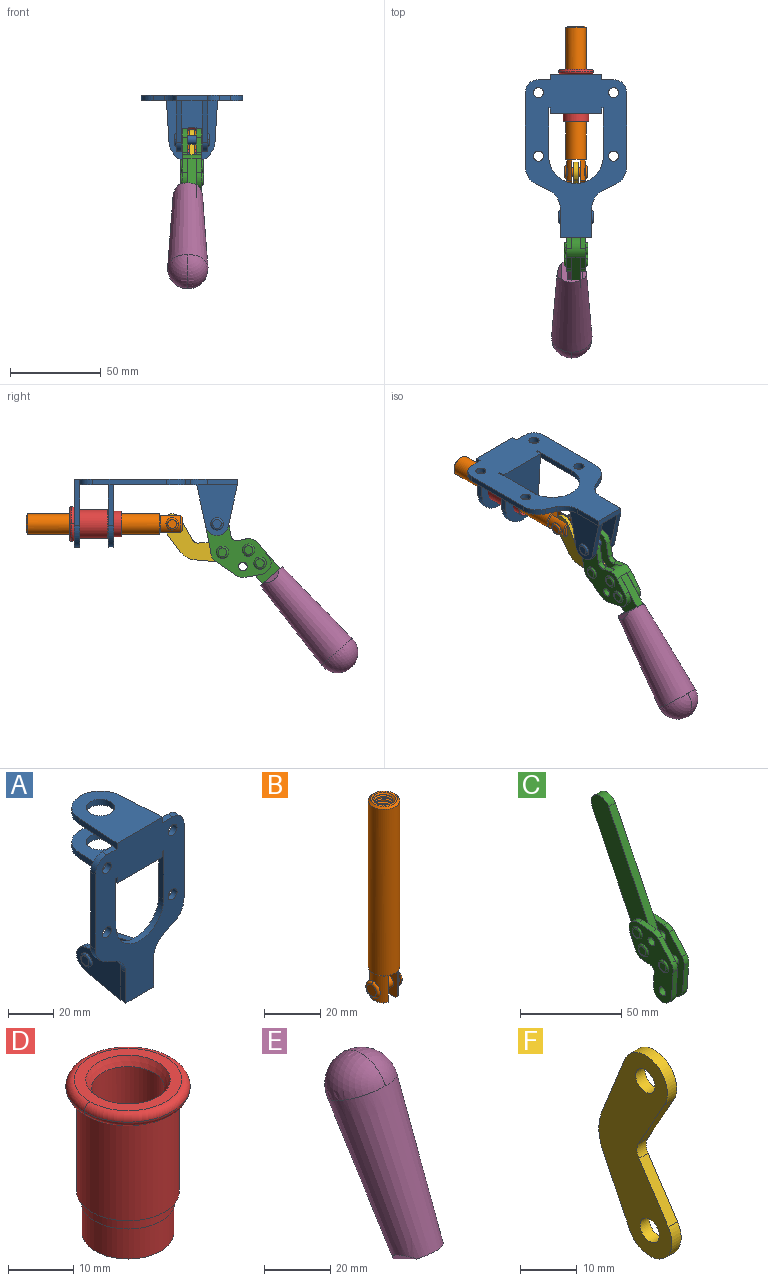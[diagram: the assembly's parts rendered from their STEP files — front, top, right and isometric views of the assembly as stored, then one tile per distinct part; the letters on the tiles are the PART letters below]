
ASSEMBLY  parts=6 mates=6
PART A: 55 faces, bbox 55.7x37.4x89.8 mm
  f0: torus R=2.41mm, axis (-1,0,0), area 15mm2, adj f11,f15,f25
  f1: torus R=2.41mm, axis (-1,0,0), area 15mm2, adj f10,f12,f22
  f2: cylinder r=2.78mm len=5.56mm, axis (0,-1,0), area 54.2mm2, adj f30,f54
  f3: cylinder r=14.99mm len=29.97mm, axis (0,-1,0), area 145.9mm2, adj f30,f49,f53,f54
  f4: cylinder r=2.78mm len=5.56mm, axis (0,-1,0), area 54.2mm2, adj f30,f54
  f5: cylinder r=2.78mm len=5.56mm, axis (0,-1,0), area 54.2mm2, adj f30,f54
  f6: cylinder r=2.78mm len=5.56mm, axis (0,-1,0), area 54.2mm2, adj f30,f54
  f7: cylinder r=6.35mm len=12.7mm, axis (0,0,1), area 123.6mm2, adj f27,f51
  f8: cylinder r=6.35mm len=12.7mm, axis (0,0,-1), area 124.7mm2, adj f21,f35
  f9: cylinder r=2.41mm len=11.18mm, axis (-1,0,0), area 169.4mm2, adj f16,f19
  f10: plane 4.83x4.83mm, normal (1,0,0), area 18.3mm2, adj f1,f12
  f11: plane 4.83x4.83mm, normal (-1,0,0), area 18.3mm2, adj f0,f15
  f12: torus R=2.41mm, axis (-1,0,0), area 15mm2, adj f1,f10,f22
  f13: cylinder r=6.35mm len=12.41mm, axis (1,0,0), area 53.4mm2, adj f18,f19,f22,f23
  f14: cylinder r=6.35mm len=12.41mm, axis (-1,0,0), area 53.4mm2, adj f16,f17,f24,f25
  f15: torus R=2.41mm, axis (-1,0,0), area 15mm2, adj f0,f11,f25
  f16: plane 27.86x22.35mm, normal (1,0,0), area 425.4mm2, adj f9,f14,f17,f24,f30
  f17: plane 22.86x4.97mm, normal (0,0.21,0.98), area 72.5mm2, adj f14,f16,f25,f30
  f18: plane 22.86x4.97mm, normal (0,0.21,0.98), area 72.5mm2, adj f13,f19,f22,f30
  f19: plane 27.86x22.35mm, normal (-1,0,0), area 425.4mm2, adj f9,f13,f18,f23,f30
  f20: cylinder r=12.7mm len=25.35mm, axis (0,0,-1), area 119.8mm2, adj f21,f34,f35,f36
  f21: plane 34.21x28.07mm, normal (0,0,-1), area 702.4mm2, adj f8,f20,f30,f34,f36
  f22: plane 27.96x22.45mm, normal (1,0,0), area 407.2mm2, adj f1,f12,f13,f18,f23,f30,f42,f43
  f23: plane 22.86x4.97mm, normal (0,0.21,-0.98), area 72.5mm2, adj f13,f19,f22,f44
  f24: plane 22.86x4.97mm, normal (0,0.21,-0.98), area 72.5mm2, adj f14,f16,f25,f44
  f25: plane 27.86x22.35mm, normal (-1,0,0), area 407.1mm2, adj f0,f14,f15,f17,f24,f30,f45,f46
  f26: plane 3.1x0.95mm, normal (0,0,-1), area 2.7mm2, adj f30,f49,f50,f54
  f27: plane 34.21x28.07mm, normal (0,0,1), area 702.4mm2, adj f7,f28,f30,f50,f52
  f28: cylinder r=12.7mm len=25.35mm, axis (0,0,1), area 118.8mm2, adj f27,f50,f51,f52
  f29: plane 3.1x0.95mm, normal (0,0,-1), area 2.7mm2, adj f30,f52,f53,f54
  f30: plane 86.54x55.63mm, normal (0,1,0), area 2362.9mm2, adj f2,f3,f4,f5,f6,f16,f17,f18
  f31: plane 40.56x3.1mm, normal (-1,0,0), area 125.7mm2, adj f30,f32,f48,f54
  f32: cylinder r=7.11mm len=7.11mm, axis (0,-1,0), area 34.6mm2, adj f30,f31,f33,f54
  f33: plane 6.67x3.1mm, normal (0,0,1), area 20.4mm2, adj f30,f32,f34,f54
  f34: plane 25.39x3.13mm, normal (-1,0.06,0), area 79.5mm2, adj f20,f21,f33,f35,f54
  f35: plane 37.31x28.45mm, normal (0,0,1), area 789.9mm2, adj f8,f20,f34,f36,f54
  f36: plane 25.39x3.13mm, normal (1,0.06,0), area 79.5mm2, adj f20,f21,f35,f37,f54
  f37: plane 6.67x3.1mm, normal (0,0,1), area 20.4mm2, adj f30,f36,f38,f54
  f38: cylinder r=7.11mm len=7.11mm, axis (0,-1,0), area 34.6mm2, adj f30,f37,f39,f54
  f39: plane 40.56x3.1mm, normal (1,0,0), area 125.7mm2, adj f30,f38,f40,f54
  f40: cylinder r=11.18mm len=10.16mm, axis (0,-1,0), area 39.5mm2, adj f30,f39,f41,f54
  f41: plane 6.09x3.1mm, normal (0.42,0,-0.91), area 20.8mm2, adj f30,f40,f42,f54
  f42: cylinder r=11.18mm len=9.41mm, axis (0,-1,0), area 37.2mm2, adj f22,f30,f41,f43,f54
  f43: plane 16.5x3.1mm, normal (1,0,0), area 51.1mm2, adj f22,f42,f44,f54
  f44: plane 17.37x3.1mm, normal (0,0,-1), area 53.8mm2, adj f23,f24,f30,f43,f45,f54
  f45: plane 16.5x3.1mm, normal (-1,0,0), area 51.1mm2, adj f25,f44,f46,f54
  f46: cylinder r=11.18mm len=9.41mm, axis (0,-1,0), area 37.2mm2, adj f25,f30,f45,f47,f54
  f47: plane 6.09x3.1mm, normal (-0.42,0,-0.91), area 20.8mm2, adj f30,f46,f48,f54
  f48: cylinder r=11.18mm len=10.16mm, axis (0,-1,0), area 39.5mm2, adj f30,f31,f47,f54
  f49: plane 26.54x3.1mm, normal (-1,0,0), area 82.3mm2, adj f3,f26,f30,f54
  f50: plane 25.39x3.1mm, normal (1,0.06,0), area 78.8mm2, adj f26,f27,f28,f51,f54
  f51: plane 37.31x28.45mm, normal (0,0,-1), area 789.9mm2, adj f7,f28,f50,f52,f54
  f52: plane 25.39x3.1mm, normal (-1,0.06,0), area 78.8mm2, adj f27,f28,f29,f51,f54
  f53: plane 26.54x3.1mm, normal (1,0,0), area 82.3mm2, adj f3,f29,f30,f54
  f54: plane 89.66x55.63mm, normal (0,-1,0), area 2678.5mm2, adj f2,f3,f4,f5,f6,f26,f29,f31
PART B: 48 faces, bbox 12.6x11.1x86.1 mm
  f0: torus R=2.41mm, axis (-1,0,0), area 15mm2, adj f30,f32,f34
  f1: torus R=2.41mm, axis (-1,0,0), area 15mm2, adj f29,f31,f33
  f2: cylinder r=5.54mm len=72.39mm, axis (0,0,1), area 2518.5mm2, adj f3,f4,f42,f43
  f3: cone r=5.54mm half-angle=45deg, axis (0,0,1), area 7.6mm2, adj f2,f5,f41
  f4: cone r=5.54mm half-angle=45deg, axis (0,0,-1), area 34.9mm2, adj f2,f39
  f5: cylinder r=5.08mm len=11.48mm, axis (0,0,1), area 108.3mm2, adj f3,f7,f8,f41
  f6: cylinder r=2.41mm len=4.83mm, axis (-1,0,0), area 71.2mm2, adj f40,f41
  f7: cylinder r=2.41mm len=4.83mm, axis (-1,0,0), area 7.6mm2, adj f5,f34
  f8: cone r=5.08mm half-angle=45deg, axis (0,0,1), area 10.6mm2, adj f5,f37,f41
  f9: cone r=3.98mm half-angle=45deg, axis (0,0,1), area 17.6mm2, adj f27,f39,f45,f46,f47
  f10: cylinder r=2.41mm len=4.83mm, axis (-1,0,0), area 7.6mm2, adj f33,f38
  f11: cylinder r=3.2mm len=6.4mm, axis (0,0,1), area 78.4mm2, adj f12,f28,f44,f45,f47
  f12: cylinder r=3.2mm len=6.4mm, axis (0,0,1), area 10.5mm2, adj f11,f13,f45,f47
  f13: cylinder r=3.2mm len=6.4mm, axis (0,0,1), area 10.5mm2, adj f12,f14,f45,f47
  f14: cylinder r=3.2mm len=6.4mm, axis (0,0,1), area 10.5mm2, adj f13,f15,f45,f47
  f15: cylinder r=3.2mm len=6.4mm, axis (0,0,1), area 10.5mm2, adj f14,f16,f45,f47
  f16: cylinder r=3.2mm len=6.4mm, axis (0,0,1), area 10.5mm2, adj f15,f17,f45,f47
  f17: cylinder r=3.2mm len=6.4mm, axis (0,0,1), area 10.5mm2, adj f16,f18,f45,f47
  f18: cylinder r=3.2mm len=6.4mm, axis (0,0,1), area 10.5mm2, adj f17,f19,f45,f47
  f19: cylinder r=3.2mm len=6.4mm, axis (0,0,1), area 10.5mm2, adj f18,f20,f45,f47
  f20: cylinder r=3.2mm len=6.4mm, axis (0,0,1), area 10.5mm2, adj f19,f21,f45,f47
  f21: cylinder r=3.2mm len=6.4mm, axis (0,0,1), area 10.5mm2, adj f20,f22,f45,f47
  f22: cylinder r=3.2mm len=6.4mm, axis (0,0,1), area 10.5mm2, adj f21,f23,f45,f47
  f23: cylinder r=3.2mm len=6.4mm, axis (0,0,1), area 10.5mm2, adj f22,f24,f45,f47
  f24: cylinder r=3.2mm len=6.4mm, axis (0,0,1), area 10.5mm2, adj f23,f25,f45,f47
  f25: cylinder r=3.2mm len=6.4mm, axis (0,0,1), area 10.5mm2, adj f24,f26,f45,f47
  f26: cylinder r=3.2mm len=6.4mm, axis (0,0,1), area 10.5mm2, adj f25,f27,f45,f47
  f27: cylinder r=3.2mm len=6.4mm, axis (0,0,1), area 7.4mm2, adj f9,f26,f45,f47
  f28: cone r=3.2mm half-angle=60deg, axis (0,0,1), area 37.2mm2, adj f11
  f29: plane 4.83x4.83mm, normal (-1,0,0), area 18.3mm2, adj f1,f31
  f30: plane 4.83x4.83mm, normal (1,0,0), area 18.3mm2, adj f0,f32
  f31: torus R=2.41mm, axis (-1,0,0), area 15mm2, adj f1,f29,f33
  f32: torus R=2.41mm, axis (-1,0,0), area 15mm2, adj f0,f30,f34
  f33: plane 6.83x6.83mm, normal (1,0,0), area 18.3mm2, adj f1,f10,f31
  f34: plane 6.83x6.83mm, normal (-1,0,0), area 18.3mm2, adj f0,f7,f32
  f35: cone r=5.08mm half-angle=45deg, axis (0,0,1), area 10.6mm2, adj f36,f38,f40
  f36: plane 7.25x1.97mm, normal (0,0,-1), area 10mm2, adj f35,f40
  f37: plane 7.25x1.97mm, normal (0,0,-1), area 10mm2, adj f8,f41
  f38: cylinder r=5.08mm len=11.48mm, axis (0,0,1), area 108.3mm2, adj f10,f35,f40,f42
  f39: plane 9.55x9.55mm, normal (0,0,1), area 22mm2, adj f4,f9
  f40: plane 12.76x10.09mm, normal (1,0,0), area 95.7mm2, adj f6,f35,f36,f38,f42,f43
  f41: plane 12.76x10.09mm, normal (-1,0,0), area 95.7mm2, adj f3,f5,f6,f8,f37,f43
  f42: cone r=5.54mm half-angle=45deg, axis (0,0,1), area 7.6mm2, adj f2,f38,f40
  f43: plane 11.07x4.7mm, normal (0,0,-1), area 50.4mm2, adj f2,f40,f41
  f44: plane 0.89x0.62mm, normal (-1,0,0), area 0.3mm2, adj f11,f45,f46,f47
  f45: bspline ~24.8x7.63mm, area 266.6mm2, adj f9,f11,f12,f13,f14,f15,f16,f17
  f46: bspline ~24.87x7.63mm, area 73.6mm2, adj f9,f44,f45,f47
  f47: bspline ~24.98x7.63mm, area 272.5mm2, adj f9,f11,f12,f13,f14,f15,f16,f17
PART C: 59 faces, bbox 12.9x60.2x99.6 mm
  f0: torus R=2.39mm, axis (-1,0,0), area 14.9mm2, adj f20,f43,f51
  f1: torus R=2.39mm, axis (-1,0,0), area 14.9mm2, adj f19,f42,f51
  f2: torus R=2.39mm, axis (-1,0,0), area 14.9mm2, adj f18,f35,f51
  f3: torus R=2.39mm, axis (-1,0,0), area 14.9mm2, adj f14,f17,f23
  f4: torus R=2.39mm, axis (-1,0,0), area 14.9mm2, adj f13,f16,f23
  f5: torus R=2.39mm, axis (-1,0,0), area 14.9mm2, adj f12,f15,f23
  f6: cylinder r=2.39mm len=4.78mm, axis (1,0,0), area 46.5mm2, adj f48,f50,f51
  f7: cylinder r=2.39mm len=4.78mm, axis (1,0,0), area 46.5mm2, adj f50,f51
  f8: cylinder r=6.35mm len=12.68mm, axis (1,0,0), area 61.8mm2, adj f38,f39,f50,f51
  f9: cylinder r=2.39mm len=4.78mm, axis (-1,0,0), area 70.5mm2, adj f46,f50
  f10: cylinder r=2.39mm len=4.78mm, axis (-1,0,0), area 46.5mm2, adj f23,f45,f46
  f11: cylinder r=2.39mm len=4.78mm, axis (-1,0,0), area 46.5mm2, adj f23,f46
  f12: plane 4.78x4.78mm, normal (1,0,0), area 17.9mm2, adj f5,f15
  f13: plane 4.78x4.78mm, normal (1,0,0), area 17.9mm2, adj f4,f16
  f14: plane 4.78x4.78mm, normal (1,0,0), area 17.9mm2, adj f3,f17
  f15: torus R=2.39mm, axis (-1,0,0), area 14.9mm2, adj f5,f12,f23
  f16: torus R=2.39mm, axis (-1,0,0), area 14.9mm2, adj f4,f13,f23
  f17: torus R=2.39mm, axis (-1,0,0), area 14.9mm2, adj f3,f14,f23
  f18: plane 4.78x4.78mm, normal (-1,0,0), area 17.9mm2, adj f2,f35
  f19: plane 4.78x4.78mm, normal (-1,0,0), area 17.9mm2, adj f1,f42
  f20: plane 4.78x4.78mm, normal (-1,0,0), area 17.9mm2, adj f0,f43
  f21: plane 2.26x0.2mm, normal (1,0,0), area 0.2mm2, adj f31,f44
  f22: plane 2.26x0.2mm, normal (-1,0,0), area 0.2mm2, adj f41,f44
  f23: plane 39.37x30.77mm, normal (1,0,0), area 565.5mm2, adj f3,f4,f5,f10,f11,f15,f16,f17
  f24: cylinder r=6.1mm len=4.15mm, axis (-1,0,0), area 14.7mm2, adj f23,f25,f32,f46
  f25: plane 10.25x9.01mm, normal (0,-0.75,0.66), area 42.3mm2, adj f23,f24,f26,f46
  f26: cylinder r=6.35mm len=4.64mm, axis (-1,0,0), area 15.6mm2, adj f23,f25,f27,f46
  f27: plane 15.84x3.1mm, normal (0,-1,-0.07), area 49.2mm2, adj f23,f26,f28,f46
  f28: cylinder r=6.35mm len=12.68mm, axis (-1,0,0), area 61.8mm2, adj f23,f27,f29,f46
  f29: plane 8.11x3.1mm, normal (0,1,0.07), area 25.2mm2, adj f23,f28,f30,f46
  f30: cylinder r=3.05mm len=3.25mm, axis (-1,0,0), area 14.8mm2, adj f23,f29,f31,f46
  f31: plane 5.99x3.1mm, normal (0,0.07,-1), area 18.6mm2, adj f21,f23,f30,f44,f46
  f32: plane 9.5x3.1mm, normal (0,-0.07,1), area 29.5mm2, adj f23,f24,f33,f46,f47
  f33: cylinder r=6.1mm len=8.63mm, axis (-1,0,0), area 39.1mm2, adj f23,f32,f34,f47
  f34: plane 8.65x3.96mm, normal (0,0.91,-0.42), area 29.5mm2, adj f23,f33,f44,f47
  f35: torus R=2.39mm, axis (-1,0,0), area 14.9mm2, adj f2,f18,f51
  f36: plane 10.25x9.01mm, normal (0,-0.75,0.66), area 42.3mm2, adj f37,f49,f50,f51
  f37: cylinder r=6.35mm len=4.64mm, axis (1,0,0), area 15.6mm2, adj f36,f38,f50,f51
  f38: plane 15.84x3.1mm, normal (0,-1,-0.07), area 49.2mm2, adj f8,f37,f50,f51
  f39: plane 8.11x3.1mm, normal (0,1,0.07), area 25.2mm2, adj f8,f40,f50,f51
  f40: cylinder r=3.05mm len=3.25mm, axis (1,0,0), area 14.8mm2, adj f39,f41,f50,f51
  f41: plane 5.99x3.1mm, normal (0,0.07,-1), area 18.6mm2, adj f22,f40,f44,f50,f51
  f42: torus R=2.39mm, axis (-1,0,0), area 14.9mm2, adj f1,f19,f51
  f43: torus R=2.39mm, axis (-1,0,0), area 14.9mm2, adj f0,f20,f51
  f44: cylinder r=6.35mm len=12.12mm, axis (-1,0,0), area 128.9mm2, adj f21,f22,f23,f31,f34,f41,f46,f47
  f45: plane 2.65x1.35mm, normal (1,0,0), area 1mm2, adj f10,f55
  f46: plane 39.08x20.42mm, normal (-1,0,0), area 412.5mm2, adj f9,f10,f11,f24,f25,f26,f27,f28
  f47: plane 77.62x39.82mm, normal (1,0,0), area 850mm2, adj f32,f33,f34,f44,f53,f54,f55
  f48: plane 2.65x1.35mm, normal (-1,0,0), area 1mm2, adj f6,f55
  f49: cylinder r=6.1mm len=4.15mm, axis (1,0,0), area 14.7mm2, adj f36,f50,f51,f56
  f50: plane 39.08x20.42mm, normal (1,0,0), area 412.5mm2, adj f6,f7,f8,f9,f36,f37,f38,f39
  f51: plane 39.37x30.77mm, normal (-1,0,0), area 565.5mm2, adj f0,f1,f2,f6,f7,f8,f35,f36
  f52: plane 8.65x3.96mm, normal (0,0.91,-0.42), area 29.5mm2, adj f44,f51,f57,f58
  f53: plane 68.49x33.4mm, normal (0,0.9,-0.44), area 358.1mm2, adj f44,f47,f54,f58
  f54: cylinder r=6.35mm len=12.06mm, axis (1,0,0), area 93.7mm2, adj f47,f53,f55,f58
  f55: plane 68.49x33.4mm, normal (0,-0.9,0.44), area 358.1mm2, adj f44,f45,f46,f47,f48,f50,f54,f58
  f56: plane 9.5x3.1mm, normal (0,-0.07,1), area 29.5mm2, adj f49,f50,f51,f57,f58
  f57: cylinder r=6.1mm len=8.63mm, axis (1,0,0), area 39.1mm2, adj f51,f52,f56,f58
  f58: plane 77.62x39.82mm, normal (-1,0,0), area 850mm2, adj f44,f52,f53,f54,f55,f56,f57
PART D: 15 faces, bbox 20.6x20.6x28.7 mm
  f0: torus R=8.26mm, axis (0,0,1), area 56.8mm2, adj f1,f10,f12
  f1: torus R=8.26mm, axis (0,0,1), area 56.8mm2, adj f0,f6,f13
  f2: cylinder r=5.59mm len=25.91mm, axis (0,0,1), area 909.6mm2, adj f3,f4
  f3: cone r=6.86mm half-angle=45deg, axis (0,0,-1), area 70.2mm2, adj f2,f14
  f4: cone r=6.47mm half-angle=30deg, axis (0,0,1), area 66.7mm2, adj f2,f13
  f5: cylinder r=7.04mm len=14.07mm, axis (0,0,1), area 252.6mm2, adj f11,f14
  f6: torus R=8.26mm, axis (0,0,1), area 56.8mm2, adj f1,f12,f13
  f7: cylinder r=7.16mm len=14.33mm, axis (0,0,1), area 91.5mm2, adj f9,f11
  f8: cylinder r=7.86mm len=18.42mm, axis (0,0,1), area 909.6mm2, adj f9,f10
  f9: plane 15.72x15.72mm, normal (0,0,-1), area 33mm2, adj f7,f8
  f10: plane 16.51x16.51mm, normal (0,0,-1), area 19.9mm2, adj f0,f8,f12
  f11: plane 14.33x14.33mm, normal (0,0,-1), area 5.7mm2, adj f5,f7
  f12: torus R=8.26mm, axis (0,0,1), area 56.8mm2, adj f0,f6,f10
  f13: plane 16.51x16.51mm, normal (0,0,1), area 82.7mm2, adj f1,f4,f6
  f14: plane 14.07x14.07mm, normal (0,0,-1), area 7.8mm2, adj f3,f5
PART E: 11 faces, bbox 22.3x42.6x64.5 mm
  f0: sphere r=11.13mm, area 411.4mm2, adj f1,f8
  f1: cone r=11.11mm half-angle=3.3deg, axis (0,0.44,0.9), area 3251.8mm2, adj f0,f7,f8,f9,f10
  f2: cylinder r=6.16mm len=11.7mm, axis (1,0,0), area 89.5mm2, adj f3,f4,f5,f6
  f3: plane 60.23x36.75mm, normal (-1,0,0), area 763.6mm2, adj f2,f4,f6,f10
  f4: plane 51.37x25.05mm, normal (0,0.9,-0.44), area 264.2mm2, adj f2,f3,f5,f10
  f5: plane 60.23x36.75mm, normal (1,0,0), area 763.6mm2, adj f2,f4,f6,f10
  f6: plane 51.37x25.05mm, normal (0,-0.9,0.44), area 264.2mm2, adj f2,f3,f5,f10
  f7: plane 9.95x5.95mm, normal (0.71,-0.31,-0.64), area 25.8mm2, adj f1,f10
  f8: sphere r=11.13mm, area 411.4mm2, adj f0,f1
  f9: plane 9.95x5.95mm, normal (-0.71,-0.31,-0.64), area 25.8mm2, adj f1,f10
  f10: plane 14.27x11.38mm, normal (0,-0.44,-0.9), area 106.7mm2, adj f1,f3,f4,f5,f6,f7,f9
PART F: 12 faces, bbox 2.3x18.2x42.8 mm
  f0: cylinder r=2.4mm len=4.8mm, axis (1,0,0), area 34.9mm2, adj f4,f11
  f1: cylinder r=10.41mm len=8.47mm, axis (1,0,0), area 20.2mm2, adj f4,f9,f10,f11
  f2: cylinder r=3.05mm len=3.16mm, axis (1,0,0), area 7.7mm2, adj f4,f6,f7,f11
  f3: cylinder r=2.4mm len=4.8mm, axis (1,0,0), area 34.9mm2, adj f4,f11
  f4: plane 42.81x18.23mm, normal (-1,0,0), area 414.1mm2, adj f0,f1,f2,f3,f5,f6,f7,f8
  f5: cylinder r=5.54mm len=10.67mm, axis (1,0,0), area 41.8mm2, adj f4,f6,f10,f11
  f6: plane 11.66x6.53mm, normal (0,-0.87,-0.49), area 30.9mm2, adj f2,f4,f5,f11
  f7: plane 11.17x7.33mm, normal (0,-0.84,0.55), area 30.9mm2, adj f2,f4,f8,f11
  f8: cylinder r=5.54mm len=10.51mm, axis (1,0,0), area 41.8mm2, adj f4,f7,f9,f11
  f9: plane 13.67x6.67mm, normal (0,0.9,-0.44), area 35.1mm2, adj f1,f4,f8,f11
  f10: plane 14.1x5.7mm, normal (0,0.93,0.37), area 35.1mm2, adj f1,f4,f5,f11
  f11: plane 42.81x18.23mm, normal (1,0,0), area 414.1mm2, adj f0,f1,f2,f3,f5,f6,f7,f8
PLACE A rot(axis=(-1,0,0),90deg) t=(0,-9.14,0)mm fixed
PLACE B rot(axis=(-1,0,0),90deg) t=(0,-32.07,0)mm
PLACE C rot(axis=(1,0,0),165deg) t=(0,-25.77,-61.98)mm
PLACE D rot(axis=(-1,0,0),90deg) t=(0,-9.14,0)mm
PLACE E rot(axis=(1,0,0),165deg) t=(-2.31,-25.77,-61.98)mm
PLACE F rot(axis=(-1,0,0),58.6deg) t=(0,-42.63,-11.66)mm
MATE fastened D.f0 <-> A.f7  axis (0,-1,0) through (0,37.25,-24.61)mm
MATE fastened E.f2 <-> C.f54  axis (1,0,0) through (0,-108.56,-96.5)mm
MATE revolute F.f3 <-> C.f4  axis (1,0,0) through (0,-44.26,-40.2)mm
MATE slider B.f2 <-> D.f2  axis (0,1,0) through (0,26.71,-24.61)mm
MATE revolute F.f5 <-> B.f6  axis (1,0,0) through (0,-16.6,-24.61)mm
MATE revolute C.f7 <-> A.f0  axis (1,0,0) through (0,-41.23,-24.61)mm
